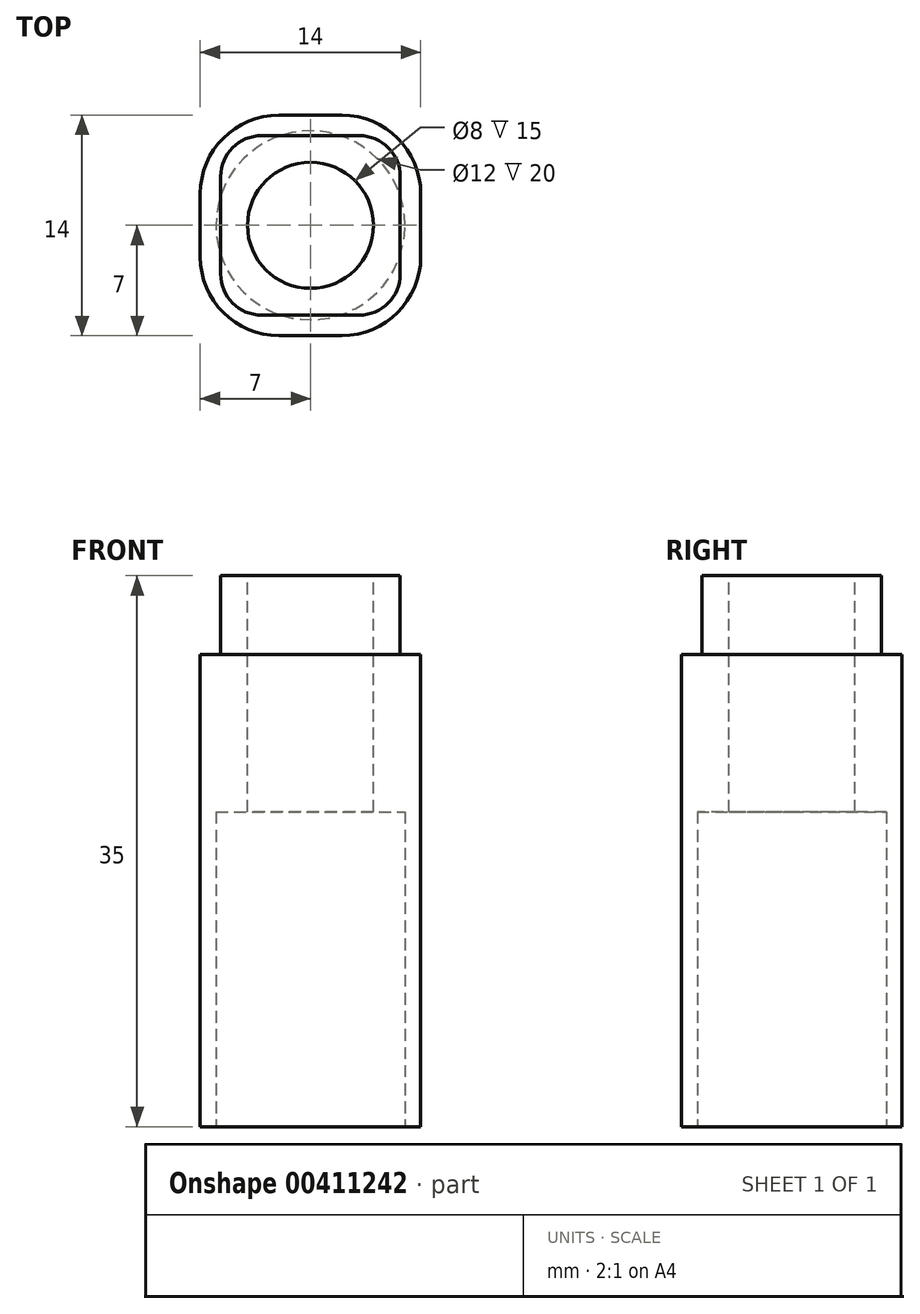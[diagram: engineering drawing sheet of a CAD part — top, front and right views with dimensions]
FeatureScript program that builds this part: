
annotation { "Feature Type Name" : "Feature", "Feature Type Description" : "" }
export const myFeature = defineFeature(function(context is Context, id is Id, definition is map)
    precondition{}
    {
        {
            var Q0;
            Q0=qCreatedBy(makeId("Top.planeOp"),FACE);
            var sketch = newSketch(context, id + "F0", { "sketchPlane" : qUnion([Q0])});
            skLineSegment(sketch, "E0.bottom", {"start": v(2, 7) * mm, "end": v(-2, 7) * mm});
            skLineSegment(sketch, "E0.top", {"start": v(2, -7) * mm, "end": v(-2, -7) * mm});
            skLineSegment(sketch, "E0.left", {"start": v(7, 2) * mm, "end": v(7, -2) * mm});
            skLineSegment(sketch, "E0.right", {"start": v(-7, 2) * mm, "end": v(-7, -2) * mm});
            skPoint(sketch, "E0.middle", {"position": v(0, 0) * mm});
            skPoint(sketch, "E1.visualSharp", {"position": v(-7, 7) * mm});
            skArc(sketch, "E1.filletArc", {"start": v(-2, 7) * mm, "mid": v(-5.54, 5.54) * mm, "end": v(-7, 2) * mm});
            skPoint(sketch, "E2.visualSharp", {"position": v(7, 7) * mm});
            skArc(sketch, "E2.filletArc", {"start": v(7, 2) * mm, "mid": v(5.54, 5.54) * mm, "end": v(2, 7) * mm});
            skPoint(sketch, "E3.visualSharp", {"position": v(7, -7) * mm});
            skArc(sketch, "E3.filletArc", {"start": v(2, -7) * mm, "mid": v(5.54, -5.54) * mm, "end": v(7, -2) * mm});
            skPoint(sketch, "E4.visualSharp", {"position": v(-7, -7) * mm});
            skArc(sketch, "E4.filletArc", {"start": v(-7, -2) * mm, "mid": v(-5.54, -5.54) * mm, "end": v(-2, -7) * mm});
            skSolve(sketch);
        }
        {
            var Q0;
            Q0=makeQuery(id+"F0.imprint","IMPRINT",FACE,{"disambiguationData":[TD([[makeQuery(id+"F0.imprint","IMPRINT",EDGE,{"derivedFrom":sQuery(id+"F0.wireOp",EDGE,"E0.bottom")}),1.0]])]});
            extrude(context, id + "F1", {"entities" : qUnion([Q0]), "depth" : 30 * mm});
        }
        {
            var Q0;
            Q0=makeQuery(id+"F1.opExtrude","CAP_FACE",FACE,{"disambiguationData":[OSD([sQuery(id+"F0.wireOp",EDGE,"E0.bottom"),sQuery(id+"F0.wireOp",EDGE,"E0.top"),sQuery(id+"F0.wireOp",EDGE,"E0.left"),sQuery(id+"F0.wireOp",EDGE,"E0.right"),sQuery(id+"F0.wireOp",EDGE,"E1.filletArc"),sQuery(id+"F0.wireOp",EDGE,"E2.filletArc"),sQuery(id+"F0.wireOp",EDGE,"E3.filletArc"),sQuery(id+"F0.wireOp",EDGE,"E4.filletArc")])],"isStart":false});
            var sketch = newSketch(context, id + "F2", { "sketchPlane" : qUnion([Q0])});
            skLineSegment(sketch, "E5.bottom", {"start": v(3.1, 5.7) * mm, "end": v(-3.1, 5.7) * mm});
            skLineSegment(sketch, "E5.top", {"start": v(3.1, -5.7) * mm, "end": v(-3.1, -5.7) * mm});
            skLineSegment(sketch, "E5.left", {"start": v(5.7, 3.1) * mm, "end": v(5.7, -3.1) * mm});
            skLineSegment(sketch, "E5.right", {"start": v(-5.7, 3.1) * mm, "end": v(-5.7, -3.1) * mm});
            skPoint(sketch, "E5.middle", {"position": v(0, 0) * mm});
            skPoint(sketch, "E6.visualSharp", {"position": v(-5.7, 5.7) * mm});
            skArc(sketch, "E6.filletArc", {"start": v(-3.1, 5.7) * mm, "mid": v(-4.94, 4.94) * mm, "end": v(-5.7, 3.1) * mm});
            skPoint(sketch, "E7.visualSharp", {"position": v(5.7, 5.7) * mm});
            skArc(sketch, "E7.filletArc", {"start": v(5.7, 3.1) * mm, "mid": v(4.94, 4.94) * mm, "end": v(3.1, 5.7) * mm});
            skPoint(sketch, "E8.visualSharp", {"position": v(5.7, -5.7) * mm});
            skArc(sketch, "E8.filletArc", {"start": v(3.1, -5.7) * mm, "mid": v(4.94, -4.94) * mm, "end": v(5.7, -3.1) * mm});
            skPoint(sketch, "E9.visualSharp", {"position": v(-5.7, -5.7) * mm});
            skArc(sketch, "E9.filletArc", {"start": v(-5.7, -3.1) * mm, "mid": v(-4.94, -4.94) * mm, "end": v(-3.1, -5.7) * mm});
            skSolve(sketch);
        }
        {
            var Q0;
            Q0=makeQuery(id+"F2.imprint","IMPRINT",FACE,{"disambiguationData":[TD([[makeQuery(id+"F2.imprint","IMPRINT",EDGE,{"derivedFrom":sQuery(id+"F2.wireOp",EDGE,"E5.bottom")}),1.0]])]});
            extrude(context, id + "F3", {"entities" : qUnion([Q0]), "operationType" : NewBodyOperationType.ADD, "depth" : 5 * mm});
        }
        {
            var Q0;
            Q0=makeQuery(id+"F3.opExtrude","CAP_FACE",FACE,{"disambiguationData":[OSD([sQuery(id+"F2.wireOp",EDGE,"E5.bottom"),sQuery(id+"F2.wireOp",EDGE,"E5.top"),sQuery(id+"F2.wireOp",EDGE,"E5.left"),sQuery(id+"F2.wireOp",EDGE,"E5.right"),sQuery(id+"F2.wireOp",EDGE,"E6.filletArc"),sQuery(id+"F2.wireOp",EDGE,"E7.filletArc"),sQuery(id+"F2.wireOp",EDGE,"E8.filletArc"),sQuery(id+"F2.wireOp",EDGE,"E9.filletArc")])],"isStart":false});
            var sketch = newSketch(context, id + "F4", { "sketchPlane" : qUnion([Q0])});
            skCircle(sketch, "E10", {"center": v(0, 0) * mm, "radius": 4 * mm});
            skSolve(sketch);
        }
        {
            var Q0;
            Q0=makeQuery(id+"F4.imprint","IMPRINT",FACE,{"disambiguationData":[TD([[makeQuery(id+"F4.imprint","IMPRINT",EDGE,{"derivedFrom":sQuery(id+"F4.wireOp",EDGE,"E10")}),1.0]])]});
            extrude(context, id + "F5", {"entities" : qUnion([Q0]), "operationType" : NewBodyOperationType.REMOVE, "oppositeDirection" : true, "depth" : 15 * mm});
        }
        {
            var Q0;
            Q0=makeQuery(id+"F1.opExtrude","CAP_FACE",FACE,{"disambiguationData":[OSD([sQuery(id+"F0.wireOp",EDGE,"E0.bottom"),sQuery(id+"F0.wireOp",EDGE,"E0.top"),sQuery(id+"F0.wireOp",EDGE,"E0.left"),sQuery(id+"F0.wireOp",EDGE,"E0.right"),sQuery(id+"F0.wireOp",EDGE,"E1.filletArc"),sQuery(id+"F0.wireOp",EDGE,"E2.filletArc"),sQuery(id+"F0.wireOp",EDGE,"E3.filletArc"),sQuery(id+"F0.wireOp",EDGE,"E4.filletArc")])],"isStart":true});
            var sketch = newSketch(context, id + "F6", { "sketchPlane" : qUnion([Q0])});
            skCircle(sketch, "E11", {"center": v(0, 0) * mm, "radius": 6 * mm});
            skSolve(sketch);
        }
        {
            var Q0;
            Q0=makeQuery(id+"F6.imprint","IMPRINT",FACE,{"disambiguationData":[TD([[makeQuery(id+"F6.imprint","IMPRINT",EDGE,{"derivedFrom":sQuery(id+"F6.wireOp",EDGE,"E11")}),1.0]])]});
            extrude(context, id + "F7", {"entities" : qUnion([Q0]), "operationType" : NewBodyOperationType.REMOVE, "oppositeDirection" : true, "depth" : 20 * mm});
        }
    });
